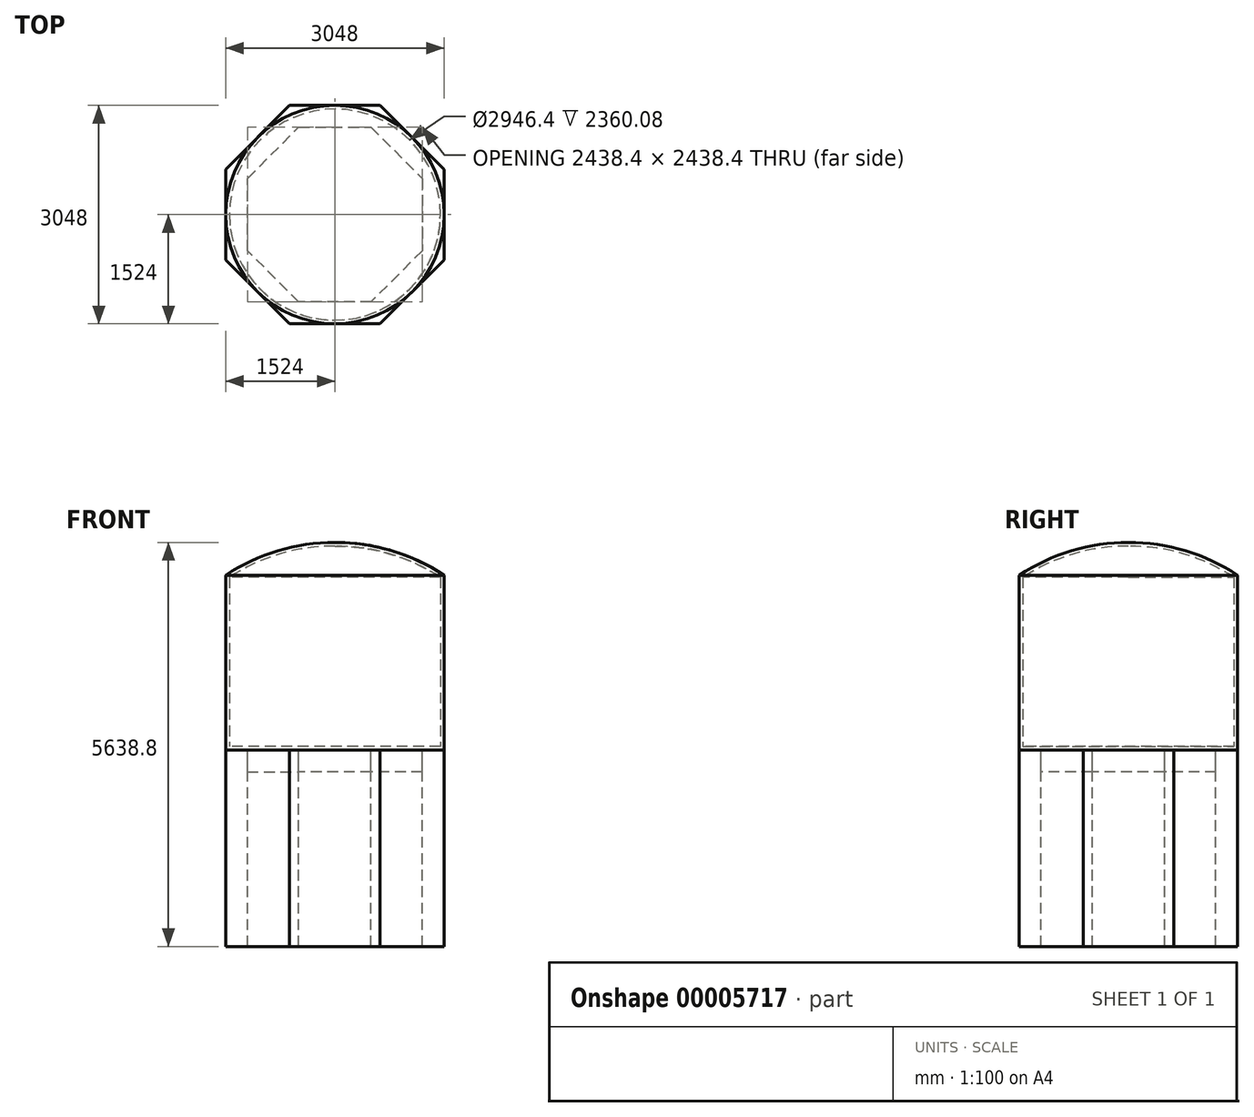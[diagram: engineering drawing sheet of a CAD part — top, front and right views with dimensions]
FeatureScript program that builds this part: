
annotation { "Feature Type Name" : "Feature", "Feature Type Description" : "" }
export const myFeature = defineFeature(function(context is Context, id is Id, definition is map)
    precondition{}
    {
        {
            var Q0;
            Q0=qCreatedBy(makeId("Top.planeOp"),FACE);
            var sketch = newSketch(context, id + "F0", { "sketchPlane" : qUnion([Q0])});
            skCircle(sketch, "E0", {"center": v(0, 0) * mm, "radius": 1524 * mm});
            skSolve(sketch);
        }
        {
            var Q0;
            Q0 = qSketchRegion(id + "F0", true);
            extrude(context, id + "F1", {"entities" : qUnion([Q0]), "depth" : 2438.4 * mm});
        }
        {
            var Q0;
            Q0=qCreatedBy(makeId("Front.planeOp"),FACE);
            var sketch = newSketch(context, id + "F2", { "sketchPlane" : qUnion([Q0])});
            skLineSegment(sketch, "E1", {"start": v(-1524, 2438.4) * mm, "end": v(0, 2438.4) * mm});
            skLineSegment(sketch, "E2", {"start": v(0, 2438.4) * mm, "end": v(0, 2895.6) * mm});
            skArc(sketch, "E3", {"start": v(0, 2895.6) * mm, "mid": v(-795.55, 2778.84) * mm, "end": v(-1524, 2438.4) * mm});
            skLineSegment(sketch, "E4", {"start": v(0, 2895.6) * mm, "end": v(431.7, 2895.6) * mm, "construction": true});
            skSolve(sketch);
        }
        {
            var Q0;
            Q0 = qSketchRegion(id + "F2", true);
            var Q1;
            Q1=sQuery(id+"F2.wireOp",EDGE,"E2");
            revolve(context, id + "F3", {"operationType" : NewBodyOperationType.ADD, "entities" : qUnion([Q0]), "axis" : qUnion([Q1]), "revolveType" : RevolveType.FULL});
        }
        {
            var Q0;
            Q0=makeQuery(id+"F1.opExtrude","CAP_FACE",FACE,{"disambiguationData":[OSD([sQuery(id+"F0.wireOp",EDGE,"E0")])],"isStart":true});
            shell(context, id + "F4", {"entities" : qUnion([Q0]), "thickness" : 50.8 * mm});
        }
        {
            var Q0;
            Q0=qCreatedBy(makeId("Top.planeOp"),FACE);
            var sketch = newSketch(context, id + "F5", { "sketchPlane" : qUnion([Q0])});
            skCircle(sketch, "E5", {"center": v(0, 0) * mm, "radius": 1524 * mm});
            skSolve(sketch);
        }
        {
            var Q0;
            Q0 = qSketchRegion(id + "F5", true);
            extrude(context, id + "F6", {"entities" : qUnion([Q0]), "operationType" : NewBodyOperationType.ADD, "depth" : 50.8 * mm});
        }
        {
            var Q0;
            Q0=qCreatedBy(makeId("Top.planeOp"),FACE);
            var sketch = newSketch(context, id + "F7", { "sketchPlane" : qUnion([Q0])});
            skCircle(sketch, "E6.cCircle", {"center": v(0, 0) * mm, "radius": 1524 * mm, "construction": true});
            skLineSegment(sketch, "E6.0", {"start": v(-1524, -631.26) * mm, "end": v(-1524, 631.26) * mm});
            skLineSegment(sketch, "E6.1", {"start": v(-1524, 631.26) * mm, "end": v(-631.26, 1524) * mm});
            skLineSegment(sketch, "E6.2", {"start": v(-631.26, 1524) * mm, "end": v(631.26, 1524) * mm});
            skLineSegment(sketch, "E6.3", {"start": v(631.26, 1524) * mm, "end": v(1524, 631.26) * mm});
            skLineSegment(sketch, "E6.4", {"start": v(1524, 631.26) * mm, "end": v(1524, -631.26) * mm});
            skLineSegment(sketch, "E6.5", {"start": v(1524, -631.26) * mm, "end": v(631.26, -1524) * mm});
            skLineSegment(sketch, "E6.6", {"start": v(631.26, -1524) * mm, "end": v(-631.26, -1524) * mm});
            skLineSegment(sketch, "E6.7", {"start": v(-631.26, -1524) * mm, "end": v(-1524, -631.26) * mm});
            skPoint(sketch, "E6.0.midPoint", {"position": v(-1524, 0) * mm});
            skCircle(sketch, "E7.cCircle", {"center": v(0, 0) * mm, "radius": 1219.2 * mm, "construction": true});
            skLineSegment(sketch, "E7.0", {"start": v(-1219.2, -505) * mm, "end": v(-1219.2, 505) * mm});
            skLineSegment(sketch, "E7.1", {"start": v(-1219.2, 505) * mm, "end": v(-505, 1219.2) * mm});
            skLineSegment(sketch, "E7.2", {"start": v(-505, 1219.2) * mm, "end": v(505, 1219.2) * mm});
            skLineSegment(sketch, "E7.3", {"start": v(505, 1219.2) * mm, "end": v(1219.2, 505) * mm});
            skLineSegment(sketch, "E7.4", {"start": v(1219.2, 505) * mm, "end": v(1219.2, -505) * mm});
            skLineSegment(sketch, "E7.5", {"start": v(1219.2, -505) * mm, "end": v(505, -1219.2) * mm});
            skLineSegment(sketch, "E7.6", {"start": v(505, -1219.2) * mm, "end": v(-505, -1219.2) * mm});
            skLineSegment(sketch, "E7.7", {"start": v(-505, -1219.2) * mm, "end": v(-1219.2, -505) * mm});
            skPoint(sketch, "E7.0.midPoint", {"position": v(-1219.2, 0) * mm});
            skSolve(sketch);
        }
        {
            var Q0;
            Q0 = qSketchRegion(id + "F7", true);
            extrude(context, id + "F8", {"entities" : qUnion([Q0]), "oppositeDirection" : true, "depth" : 2743.2 * mm});
        }
        {
            var Q0;
            Q0=qCreatedBy(makeId("Top.planeOp"),FACE);
            var sketch = newSketch(context, id + "F9", { "sketchPlane" : qUnion([Q0])});
            skLineSegment(sketch, "E8.0", {"start": v(505, -1219.2) * mm, "end": v(-505, -1219.2) * mm});
            skLineSegment(sketch, "E9.0", {"start": v(-505, -1219.2) * mm, "end": v(-1219.2, -505) * mm});
            skLineSegment(sketch, "E9.1", {"start": v(-1219.2, 505) * mm, "end": v(-505, 1219.2) * mm});
            skLineSegment(sketch, "E9.2", {"start": v(-1219.2, -505) * mm, "end": v(-1219.2, 505) * mm});
            skLineSegment(sketch, "E9.3", {"start": v(-505, 1219.2) * mm, "end": v(505, 1219.2) * mm});
            skLineSegment(sketch, "E9.4", {"start": v(505, 1219.2) * mm, "end": v(1219.2, 505) * mm});
            skLineSegment(sketch, "E9.5", {"start": v(1219.2, 505) * mm, "end": v(1219.2, -505) * mm});
            skLineSegment(sketch, "E9.6", {"start": v(1219.2, -505) * mm, "end": v(505, -1219.2) * mm});
            skSolve(sketch);
        }
        {
            var Q0;
            Q0 = qSketchRegion(id + "F9", true);
            extrude(context, id + "F10", {"entities" : qUnion([Q0]), "oppositeDirection" : true, "depth" : 304.8 * mm});
        }
        {
            var Q0;
            Q0=makeQuery(id+"F10.opExtrude","CAP_FACE",FACE,{"disambiguationData":[OSD([sQuery(id+"F9.wireOp",EDGE,"E8.0"),sQuery(id+"F9.wireOp",EDGE,"E9.0"),sQuery(id+"F9.wireOp",EDGE,"E9.1"),sQuery(id+"F9.wireOp",EDGE,"E9.2"),sQuery(id+"F9.wireOp",EDGE,"E9.3"),sQuery(id+"F9.wireOp",EDGE,"E9.4"),sQuery(id+"F9.wireOp",EDGE,"E9.5"),sQuery(id+"F9.wireOp",EDGE,"E9.6")])],"isStart":false});
            var sketch = newSketch(context, id + "F11", { "sketchPlane" : qUnion([Q0])});
            skCircle(sketch, "E10.cCircle", {"center": v(0, 0) * mm, "radius": 1219.2 * mm, "construction": true});
            skLineSegment(sketch, "E10.0", {"start": v(-505, -1219.2) * mm, "end": v(-1219.2, -505) * mm});
            skLineSegment(sketch, "E10.1", {"start": v(-1219.2, -505) * mm, "end": v(-1219.2, 505) * mm});
            skLineSegment(sketch, "E10.2", {"start": v(-1219.2, 505) * mm, "end": v(-505, 1219.2) * mm});
            skLineSegment(sketch, "E10.3", {"start": v(-505, 1219.2) * mm, "end": v(505, 1219.2) * mm});
            skLineSegment(sketch, "E10.4", {"start": v(505, 1219.2) * mm, "end": v(1219.2, 505) * mm});
            skLineSegment(sketch, "E10.5", {"start": v(1219.2, 505) * mm, "end": v(1219.2, -505) * mm});
            skLineSegment(sketch, "E10.6", {"start": v(1219.2, -505) * mm, "end": v(505, -1219.2) * mm});
            skLineSegment(sketch, "E10.7", {"start": v(505, -1219.2) * mm, "end": v(-505, -1219.2) * mm});
            skPoint(sketch, "E10.0.midPoint", {"position": v(-862.1, -862.1) * mm});
            skSolve(sketch);
        }
        {
            var Q0;
            Q0 = qSketchRegion(id + "F11", true);
            var Q1;
            Q1=makeQuery(id+"F8.opExtrude","CAP_FACE",FACE,{"disambiguationData":[OSD([sQuery(id+"F7.wireOp",EDGE,"E6.0"),sQuery(id+"F7.wireOp",EDGE,"E6.1"),sQuery(id+"F7.wireOp",EDGE,"E6.2"),sQuery(id+"F7.wireOp",EDGE,"E6.3"),sQuery(id+"F7.wireOp",EDGE,"E6.4"),sQuery(id+"F7.wireOp",EDGE,"E6.5"),sQuery(id+"F7.wireOp",EDGE,"E6.6"),sQuery(id+"F7.wireOp",EDGE,"E6.7"),sQuery(id+"F7.wireOp",EDGE,"E7.0"),sQuery(id+"F7.wireOp",EDGE,"E7.1"),sQuery(id+"F7.wireOp",EDGE,"E7.2"),sQuery(id+"F7.wireOp",EDGE,"E7.3"),sQuery(id+"F7.wireOp",EDGE,"E7.4"),sQuery(id+"F7.wireOp",EDGE,"E7.5"),sQuery(id+"F7.wireOp",EDGE,"E7.6"),sQuery(id+"F7.wireOp",EDGE,"E7.7")])],"isStart":false});
            extrude(context, id + "F12", {"entities" : qUnion([Q0]), "endBound" : BoundingType.UP_TO_SURFACE, "endBoundEntityFace" : qUnion([Q1]), "depth" : 30.48 * mm});
        }
    });
